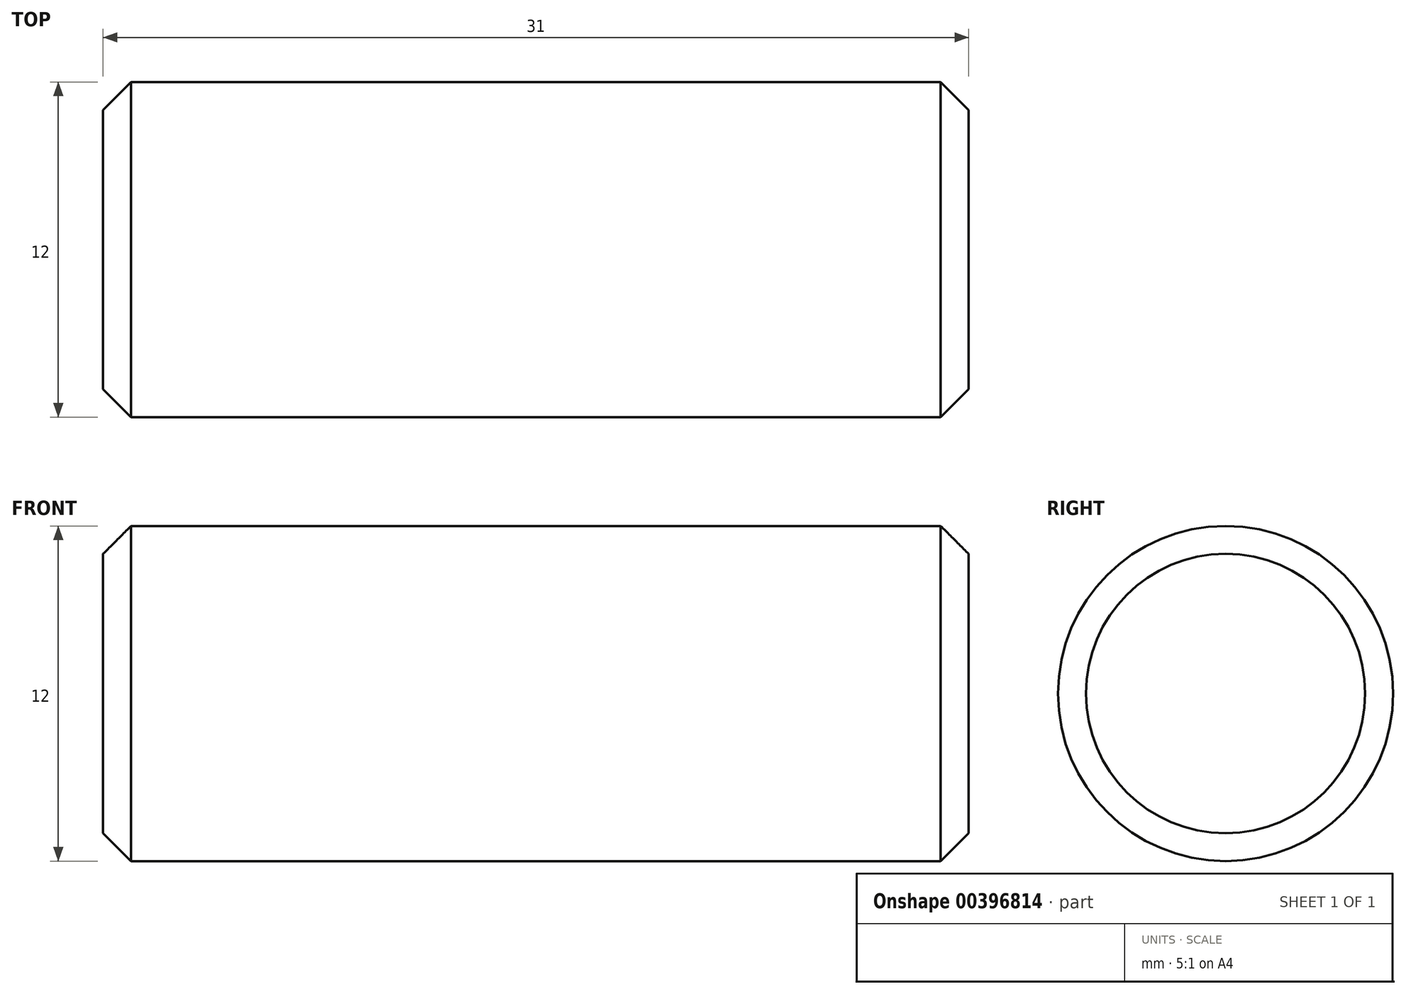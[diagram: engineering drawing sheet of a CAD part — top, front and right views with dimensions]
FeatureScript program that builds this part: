
annotation { "Feature Type Name" : "Feature", "Feature Type Description" : "" }
export const myFeature = defineFeature(function(context is Context, id is Id, definition is map)
    precondition{}
    {
        {
            var Q0;
            Q0=qCreatedBy(makeId("Front.planeOp"),FACE);
            var sketch = newSketch(context, id + "F0", { "sketchPlane" : qUnion([Q0])});
            skLineSegment(sketch, "E0.bottom", {"start": v(0, 0) * mm, "end": v(31, 0) * mm});
            skLineSegment(sketch, "E0.top", {"start": v(0, 6) * mm, "end": v(31, 6) * mm});
            skLineSegment(sketch, "E0.left", {"start": v(0, 0) * mm, "end": v(0, 6) * mm});
            skLineSegment(sketch, "E0.right", {"start": v(31, 0) * mm, "end": v(31, 6) * mm});
            skSolve(sketch);
        }
        {
            var Q0;
            Q0=makeQuery(id+"F0.imprint","IMPRINT",FACE,{"disambiguationData":[TD([[makeQuery(id+"F0.imprint","IMPRINT",EDGE,{"derivedFrom":sQuery(id+"F0.wireOp",EDGE,"E0.bottom")}),1.0]])]});
            var Q1;
            Q1=sQuery(id+"F0.wireOp",EDGE,"E0.bottom");
            revolve(context, id + "F1", {"entities" : qUnion([Q0]), "axis" : qUnion([Q1]), "revolveType" : RevolveType.FULL});
        }
        {
            var Q0;
            Q0=makeQuery(id+"F1.opRevolve","SWEPT_EDGE",EDGE,{"disambiguationData":[OSD([sQuery(id+"F0.wireOp",EDGE,"E0.top"),sQuery(id+"F0.wireOp",EDGE,"E0.right")])]});
            var Q1;
            Q1=makeQuery(id+"F1.opRevolve","SWEPT_EDGE",EDGE,{"disambiguationData":[OSD([sQuery(id+"F0.wireOp",EDGE,"E0.top"),sQuery(id+"F0.wireOp",EDGE,"E0.left")])]});
            chamfer(context, id + "F2", {"entities" : qUnion([Q0, Q1]), "width" : 1 * mm, "tangentPropagation" : true});
        }
    });
